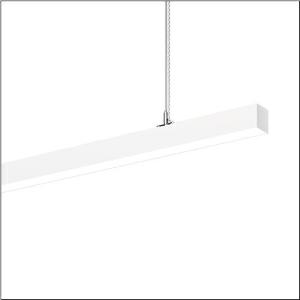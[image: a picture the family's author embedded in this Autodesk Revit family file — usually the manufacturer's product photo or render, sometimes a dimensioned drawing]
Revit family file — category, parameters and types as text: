
# Revit family: silica_21_51mx30da34wb
name_source: partatom
category: Lighting Fixtures
units: mm (PartAtom-declared; Revit-internal decimal feet)

## family parameters
Cut with Voids When Loaded = No
Host = Face
Light Source = No
Part Type = Normal
Room Calculation Point = No
Round Connector Dimension = Use Diameter
Shared = No

## types (1)
- --- (1 x LED, 4210 lm, 27.7 W, 3000K)
    Apparent Load = 28 VA
    CIE Flux Codes = 47 79 96 57 100
    Color Rendering = 80
    Color Temperature = 3000K
    Default Elevation = 1800 mm
    Description = Silica 21, office luminaire, primary optical cover: cover, of PMMA, opal, light emission: direct/indirect distribution, primary light characteristic: symmetric, installation type: suspended mounting, LED, rated luminous flux: 4.210lm, luminous efficacy: 152lm/W, light colour: 830, colour temperature: 3000K, control gear: DALI 2, with terminal, 3+2-pole, max. 2.5mm², mains connection: 220..240V, AC, 50/60Hz, rated input power: 27.7W, luminaire housing, of aluminium, traffic white (RAL 9016), length: 1.204mm, width: 53mm, height: 53mm, protection rating (complete): IP20, insulation class (complete): insulation class I (protective earthing), certification: CE, permissible operating ambient temperature: 0..+35°C, standard: EN 50419, packaging unit: 1 piece
    Height = 53 mm
    Lamp = 1 x LED
    Lamp Light Flux = 4210 lm
    Lamp Power = 27.7 W
    Lamp count = 1
    Length = 1204 mm
    Luminous efficacy = 152 lm/W
    Manufacturer = Siteco
    ModVariant = No
    Model = 51MX30DA34WB
    Mounting Place = Ceiling
    Mounting Type = Pendant
    Number of Poles = 1
    OnlyDefault = Yes
    Power Factor = 1
    Product Name = Silica 21
    Product group = office luminaire | ceiling pendant
    ProductGroupID = 903
    Protection Class = Protection class I
    Protection Degree = IP 20
    RLX_Detail_Level = 1
    RLX_Emergency_Light_Flux = 0 lm
    RLX_Emergency_Type = 0
    RLX_Emergency_Type_DB = No
    RlxData = <blob elided: 20689 chars, md5=f9b2303f>
    Socket = socket
    Standby Power = 0 W
    System Light Flux = 4210 lm
    System Power = 28 W
    Type Comments = factory setting: luminous flux: 100 % | dim-lin: 254 | 233 mA
    Type Image = l_1349023.jpg
    URL = http://relux.com
    VarID = @adj_119197
    Voltage = 0 V
    Weight = 0.00 kg
    Width = 53 mm

## geometry (parser evidence)
native form markers: Blend x4, Sweep x13
no freeform markers — native parametric forms only
